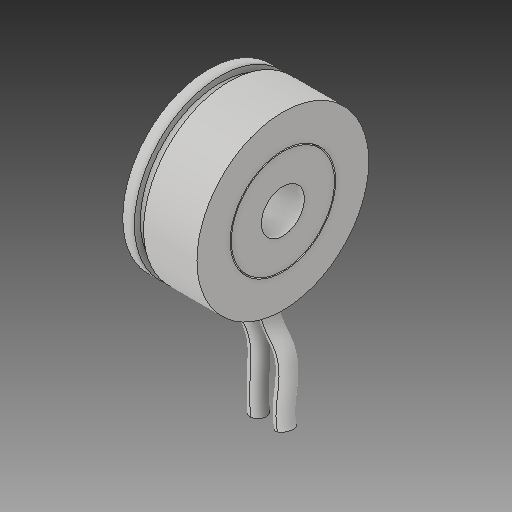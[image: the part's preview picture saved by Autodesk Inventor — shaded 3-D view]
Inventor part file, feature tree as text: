
AUTODESK INVENTOR PART (.ipt)
format: ipt  version: 2019 (Build 230136000, 136)  size: 275,968 bytes
history: native  units: in
note: dims shown in document units (in); Inventor stores cm internally (conversion verified against a paired STEP export)
features: sweep x2, revolve x1, other x1
ambient origin geometry x8: Origin, YZ Plane, XZ Plane, XY Plane, X Axis, Y Axis, Z Axis, Center Point
bodies: Solid1 (feature_tree), Solid2 (feature_tree), Solid3 (feature_tree), Solid4 (feature_tree)
feature tree (4):
  revolve  "Revolve1[2]"  [1 undecoded]
  other  "Boss-Extrude1"
  sweep  "Sweep1"
  sweep  "Sweep2"
note: 1 required parameter value undecoded (feature->parameter linkage not recoverable at this tier; creation-order binding heuristic only, values carry confidence <= 0.55)
